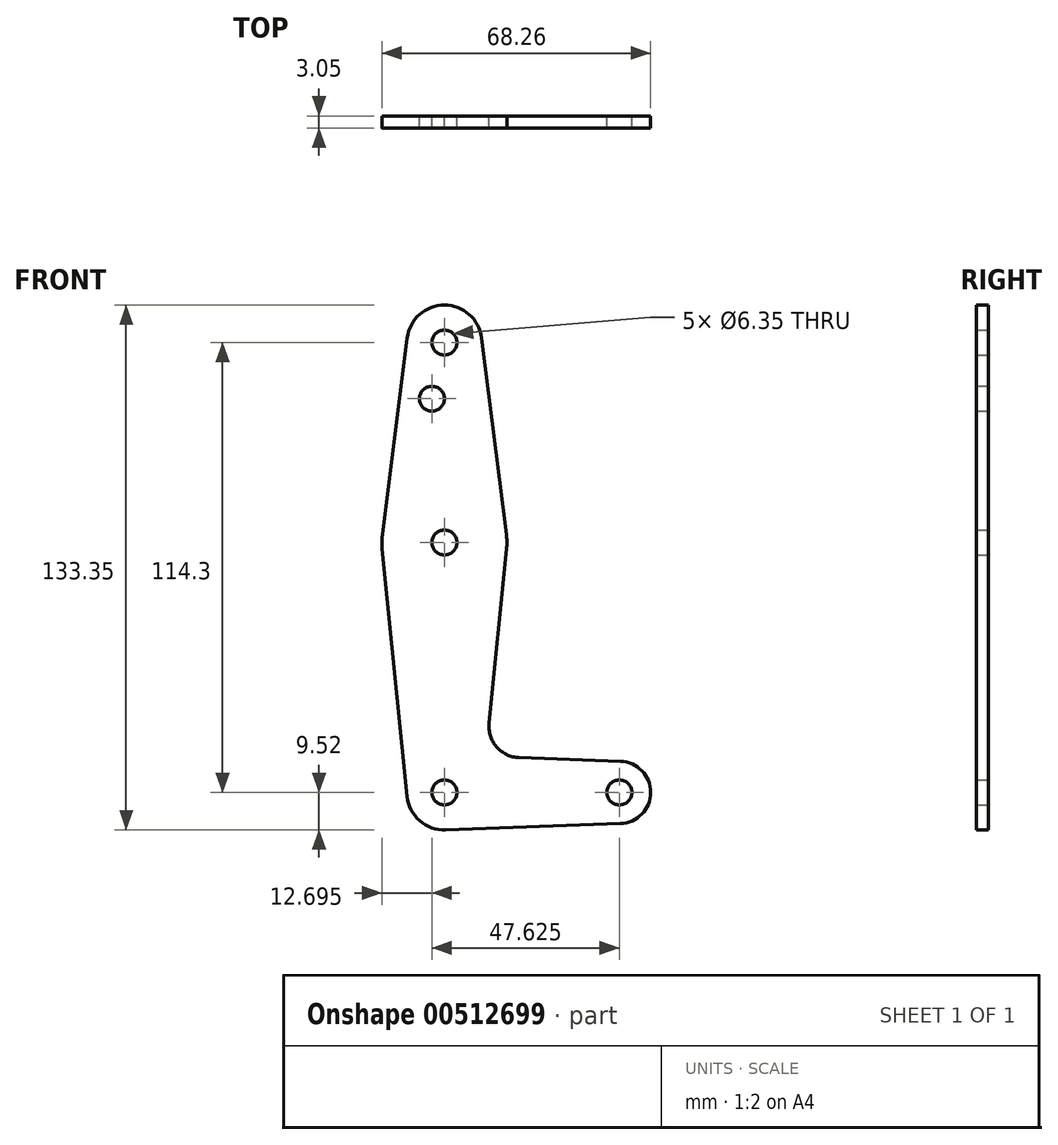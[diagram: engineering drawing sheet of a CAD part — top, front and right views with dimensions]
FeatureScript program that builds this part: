
annotation { "Feature Type Name" : "Feature", "Feature Type Description" : "" }
export const myFeature = defineFeature(function(context is Context, id is Id, definition is map)
    precondition{}
    {
        {
            var Q0;
            Q0=qCreatedBy(makeId("Front.planeOp"),FACE);
            var sketch = newSketch(context, id + "F0", { "sketchPlane" : qUnion([Q0])});
            skCircle(sketch, "E0", {"center": v(0, 0) * mm, "radius": 9.53 * mm});
            skCircle(sketch, "E1", {"center": v(0, 63.5) * mm, "radius": 15.88 * mm});
            skCircle(sketch, "E2", {"center": v(0, 114.3) * mm, "radius": 9.53 * mm});
            skCircle(sketch, "E3", {"center": v(44.45, 0) * mm, "radius": 7.94 * mm});
            skLineSegment(sketch, "E4", {"start": v(44.45, 0) * mm, "end": v(0, 0) * mm, "construction": true});
            skLineSegment(sketch, "E5", {"start": v(0, 0) * mm, "end": v(0, 114.3) * mm, "construction": true});
            skLineSegment(sketch, "E6", {"start": v(-9.45, 115.5) * mm, "end": v(-15.75, 65.48) * mm});
            skLineSegment(sketch, "E7", {"start": v(15.75, 65.48) * mm, "end": v(9.45, 115.5) * mm});
            skLineSegment(sketch, "E8", {"start": v(44.73, 7.93) * mm, "end": v(18.97, 8.85) * mm});
            skLineSegment(sketch, "E9", {"start": v(44.73, -7.93) * mm, "end": v(0, -9.53) * mm});
            skLineSegment(sketch, "E10", {"start": v(-9.48, -0.95) * mm, "end": v(-15.8, 61.91) * mm});
            skLineSegment(sketch, "E11", {"start": v(15.8, 61.91) * mm, "end": v(11.34, 17.6) * mm});
            skCircle(sketch, "E12", {"center": v(0, 114.3) * mm, "radius": 3.18 * mm});
            skCircle(sketch, "E13", {"center": v(0, 63.5) * mm, "radius": 3.18 * mm});
            skCircle(sketch, "E14", {"center": v(0, 0) * mm, "radius": 3.18 * mm});
            skCircle(sketch, "E15", {"center": v(44.45, 0) * mm, "radius": 3.18 * mm});
            skCircle(sketch, "E16", {"center": v(-3.18, 100.03) * mm, "radius": 3.18 * mm});
            skPoint(sketch, "E17.newPointB", {"position": v(0, 9.53) * mm});
            skArc(sketch, "E17.filletArc", {"start": v(11.34, 17.6) * mm, "mid": v(13.26, 11.57) * mm, "end": v(18.97, 8.85) * mm});
            skSolve(sketch);
        }
        {
            var Q0;
            Q0 = qSketchRegion(id + "F0", true);
            extrude(context, id + "F1", {"entities" : qUnion([Q0]), "depth" : 3.05 * mm});
        }
    });
